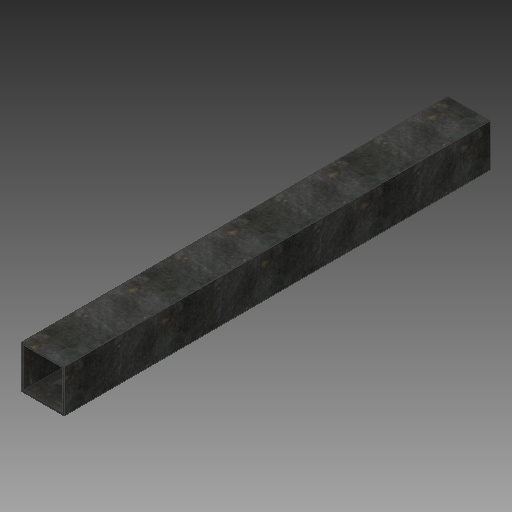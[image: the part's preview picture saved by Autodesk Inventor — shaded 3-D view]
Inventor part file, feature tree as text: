
AUTODESK INVENTOR PART (.ipt)
format: ipt  version: 2018 (Build 220112000, 112)  size: 162,304 bytes
history: native  units: mm
features: other x1, extrude x1, sketch x1
ambient origin geometry x8: Origin, YZ Plane, XZ Plane, XY Plane, X Axis, Y Axis, Z Axis, Center Point
bodies: Body1 (feature_tree)
feature tree (3):
  other  "Sólido1"
  extrude  "Extrusión1"  Depth=75.0mm
  sketch  "Boceto1"  dims[d0=75.0mm d1=75.0mm d2=3.0mm d3=37.5mm d4=37.5mm d5=750.0mm d6=0.0mm]
